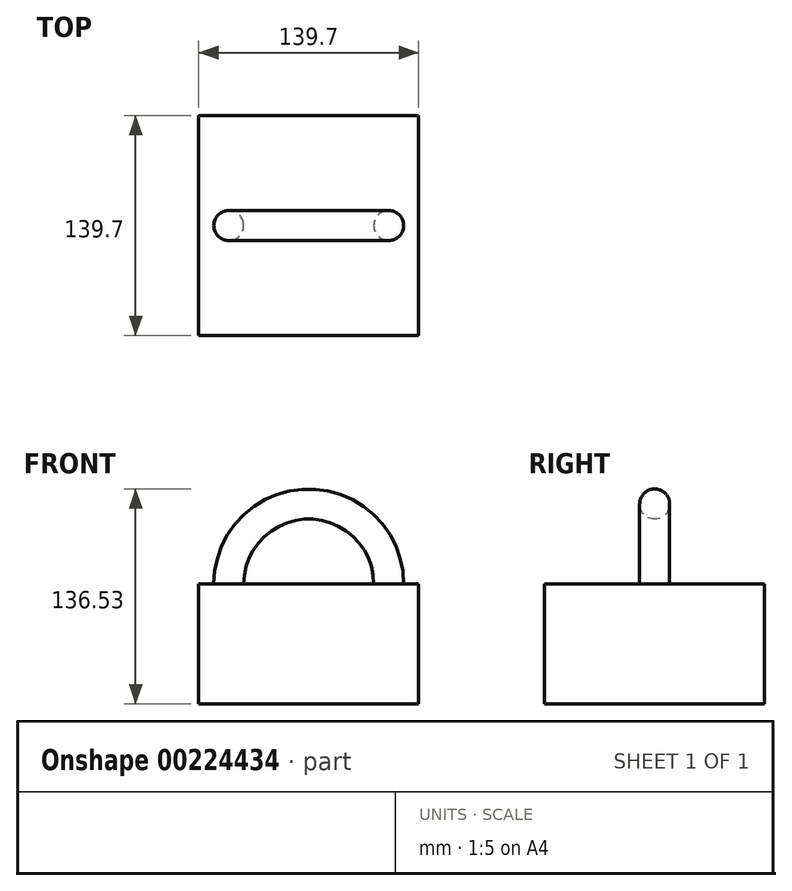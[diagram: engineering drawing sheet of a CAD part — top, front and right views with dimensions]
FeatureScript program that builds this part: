
annotation { "Feature Type Name" : "Feature", "Feature Type Description" : "" }
export const myFeature = defineFeature(function(context is Context, id is Id, definition is map)
    precondition{}
    {
        {
            var Q0;
            Q0=qCreatedBy(makeId("Top.planeOp"),FACE);
            var sketch = newSketch(context, id + "F0", { "sketchPlane" : qUnion([Q0])});
            skLineSegment(sketch, "E0.bottom", {"start": v(0, -69.85) * mm, "end": v(-69.85, -69.85) * mm});
            skLineSegment(sketch, "E0.top", {"start": v(0, 69.85) * mm, "end": v(-69.85, 69.85) * mm});
            skLineSegment(sketch, "E0.left", {"start": v(0, -69.85) * mm, "end": v(0, 69.85) * mm});
            skLineSegment(sketch, "E0.right", {"start": v(-69.85, -69.85) * mm, "end": v(-69.85, 69.85) * mm});
            skLineSegment(sketch, "E1.bottom", {"start": v(0, 69.85) * mm, "end": v(69.85, 69.85) * mm});
            skLineSegment(sketch, "E1.top", {"start": v(0, -69.85) * mm, "end": v(69.85, -69.85) * mm});
            skLineSegment(sketch, "E1.left", {"start": v(0, 69.85) * mm, "end": v(0, -69.85) * mm});
            skLineSegment(sketch, "E1.right", {"start": v(69.85, 69.85) * mm, "end": v(69.85, -69.85) * mm});
            skSolve(sketch);
        }
        {
            var Q0;
            Q0=qCreatedBy(makeId("Top.planeOp"),FACE);
            var sketch = newSketch(context, id + "F1", { "sketchPlane" : qUnion([Q0])});
            skCircle(sketch, "E2", {"center": v(50.8, 0) * mm, "radius": 9.53 * mm});
            skLineSegment(sketch, "E3", {"start": v(0, 63.91) * mm, "end": v(0, -60.51) * mm});
            skSolve(sketch);
        }
        {
            var Q0;
            Q0=makeQuery(id+"F0.imprint","IMPRINT",FACE,{"disambiguationData":[TD([[makeQuery(id+"F0.imprint","IMPRINT",EDGE,{"derivedFrom":sQuery(id+"F0.wireOp",EDGE,"E0.bottom")}),-1.0]])]});
            var Q1;
            Q1=makeQuery(id+"F0.imprint","IMPRINT",FACE,{"disambiguationData":[TD([[makeQuery(id+"F0.imprint","IMPRINT",EDGE,{"derivedFrom":sQuery(id+"F0.wireOp",EDGE,"E1.bottom")}),-1.0]])]});
            extrude(context, id + "F2", {"entities" : qUnion([Q0, Q1]), "oppositeDirection" : true, "depth" : 76.2 * mm});
        }
        {
            var Q0;
            Q0=makeQuery(id+"F1.imprint","IMPRINT",FACE,{"disambiguationData":[TD([[makeQuery(id+"F1.imprint","IMPRINT",EDGE,{"derivedFrom":sQuery(id+"F1.wireOp",EDGE,"E2")}),1.0]])]});
            var Q1;
            Q1=sQuery(id+"F1.wireOp",EDGE,"E3");
            revolve(context, id + "F3", {"operationType" : NewBodyOperationType.ADD, "entities" : qUnion([Q0]), "axis" : qUnion([Q1]), "revolveType" : RevolveType.FULL});
        }
    });
